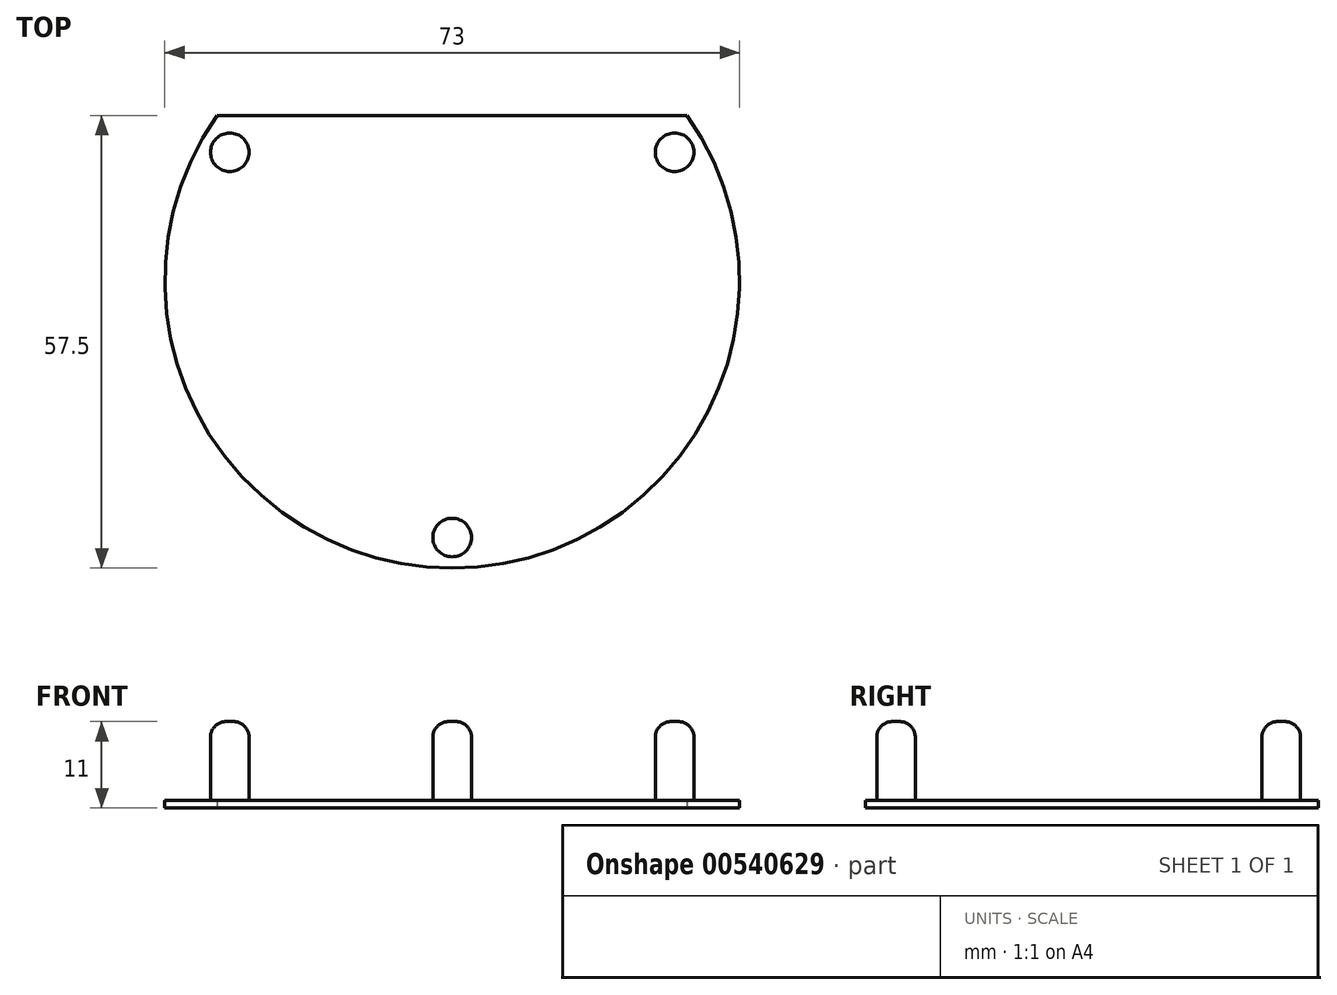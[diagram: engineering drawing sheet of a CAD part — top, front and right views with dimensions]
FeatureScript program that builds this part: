
annotation { "Feature Type Name" : "Feature", "Feature Type Description" : "" }
export const myFeature = defineFeature(function(context is Context, id is Id, definition is map)
    precondition{}
    {
        {
            var Q0;
            Q0=qCreatedBy(makeId("Top.planeOp"),FACE);
            var sketch = newSketch(context, id + "F0", { "sketchPlane" : qUnion([Q0])});
            skArc(sketch, "E0", {"start": v(-29.85, 21) * mm, "mid": v(0, -36.5) * mm, "end": v(29.85, 21) * mm});
            skLineSegment(sketch, "E1", {"start": v(-29.85, 21) * mm, "end": v(29.85, 21) * mm});
            skSolve(sketch);
        }
        {
            var Q0;
            Q0=makeQuery(id+"F0.imprint","IMPRINT",FACE,{"disambiguationData":[TD([[makeQuery(id+"F0.imprint","IMPRINT",EDGE,{"derivedFrom":sQuery(id+"F0.wireOp",EDGE,"E0")}),1.0]])]});
            extrude(context, id + "F1", {"entities" : qUnion([Q0]), "depth" : 1 * mm, "offsetDistance" : 25 * mm});
        }
        {
            var Q0;
            Q0=makeQuery(id+"F1.opExtrude","CAP_FACE",FACE,{"disambiguationData":[OSD([sQuery(id+"F0.wireOp",EDGE,"E0"),sQuery(id+"F0.wireOp",EDGE,"E1")])],"isStart":false});
            var sketch = newSketch(context, id + "F2", { "sketchPlane" : qUnion([Q0])});
            skCircle(sketch, "E2", {"center": v(0, -32.62) * mm, "radius": 2.45 * mm});
            skCircle(sketch, "E3.1.0", {"center": v(28.25, 16.31) * mm, "radius": 2.45 * mm});
            skCircle(sketch, "E3.2.0", {"center": v(-28.25, 16.31) * mm, "radius": 2.45 * mm});
            skPoint(sketch, "E3.center", {"position": v(0, 0) * mm});
            skSolve(sketch);
        }
        {
            var Q0;
            Q0 = qSketchRegion(id + "F2", true);
            var Q1;
            Q1=sQuery(id+"F2.wireOp",EDGE,"E3.2.0");
            var Q2;
            Q2=sQuery(id+"F2.wireOp",EDGE,"E3.1.0");
            var Q3;
            Q3=sQuery(id+"F2.wireOp",EDGE,"E2");
            extrude(context, id + "F3", {"entities" : qUnion([Q0]), "operationType" : NewBodyOperationType.ADD, "surfaceEntities" : qUnion([Q1, Q2, Q3]), "depth" : 10 * mm, "offsetDistance" : 25 * mm});
        }
        {
            var Q0;
            Q0=makeQuery(id+"F3.opExtrude","CAP_EDGE",EDGE,{"disambiguationData":[OSD([sQuery(id+"F2.wireOp",EDGE,"E3.2.0")])],"isStart":false});
            var Q1;
            Q1=makeQuery(id+"F3.opExtrude","CAP_EDGE",EDGE,{"disambiguationData":[OSD([sQuery(id+"F2.wireOp",EDGE,"E3.1.0")])],"isStart":false});
            var Q2;
            Q2=makeQuery(id+"F3.opExtrude","CAP_EDGE",EDGE,{"disambiguationData":[OSD([sQuery(id+"F2.wireOp",EDGE,"E2")])],"isStart":false});
            var Q3;
            Q3=makeQuery(id+"F3.opExtrude","CAP_EDGE",EDGE,{"disambiguationData":[OSD([sQuery(id+"F2.wireOp",EDGE,"E3.2.0")])],"isStart":true});
            var Q4;
            Q4=makeQuery(id+"F3.opExtrude","CAP_EDGE",EDGE,{"disambiguationData":[OSD([sQuery(id+"F2.wireOp",EDGE,"E3.1.0")])],"isStart":true});
            var Q5;
            Q5=makeQuery(id+"F3.opExtrude","CAP_EDGE",EDGE,{"disambiguationData":[OSD([sQuery(id+"F2.wireOp",EDGE,"E2")])],"isStart":true});
            fillet(context, id + "F4", {"entities" : qUnion([Q0, Q1, Q2, Q3, Q4, Q5]), "radius" : 2 * mm, "tangentPropagation" : true, "allowEdgeOverflow" : false});
        }
    });
